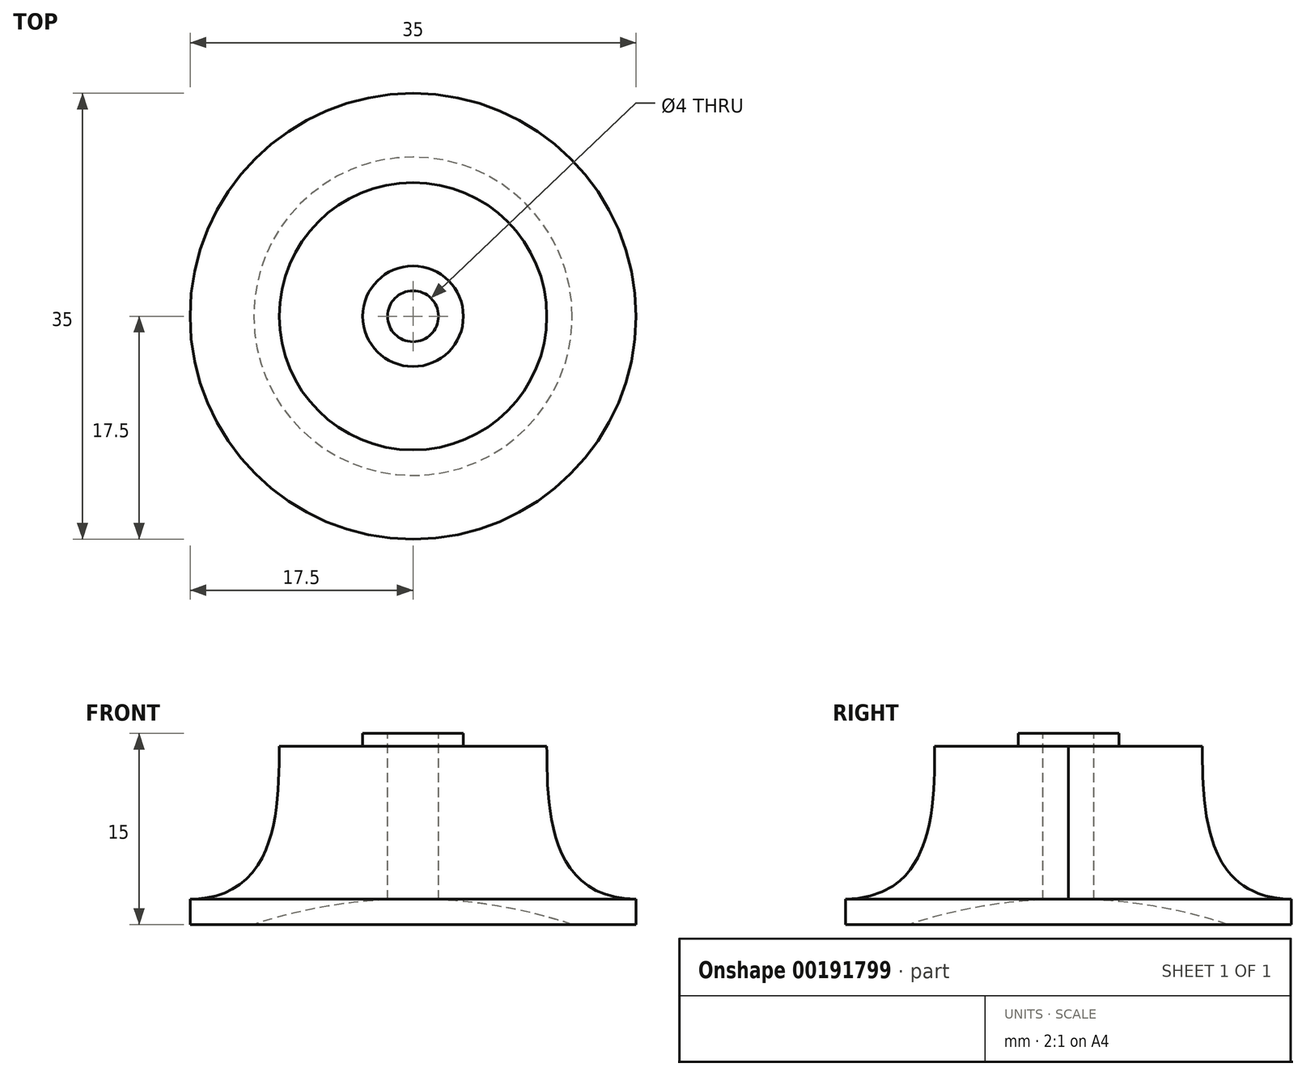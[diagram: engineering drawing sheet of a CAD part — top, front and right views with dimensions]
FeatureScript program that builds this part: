
annotation { "Feature Type Name" : "Feature", "Feature Type Description" : "" }
export const myFeature = defineFeature(function(context is Context, id is Id, definition is map)
    precondition{}
    {
        {
            var Q0;
            Q0=qCreatedBy(makeId("Front.planeOp"),FACE);
            var sketch = newSketch(context, id + "F0", { "sketchPlane" : qUnion([Q0])});
            skLineSegment(sketch, "E0", {"start": v(0, 14) * mm, "end": v(10.5, 14) * mm});
            skLineSegment(sketch, "E1", {"start": v(0, 14) * mm, "end": v(0, 0) * mm});
            skLineSegment(sketch, "E2", {"start": v(0, 2) * mm, "end": v(17.5, 2) * mm});
            skLineSegment(sketch, "E3", {"start": v(17.5, 2) * mm, "end": v(17.5, 0) * mm});
            skFitSpline(sketch, "E4", {"points": [v(17.5, 2) * mm, v(10.5, 14) * mm], "startDerivative": vector(-21.74, 0) * mm, "endDerivative": vector(-0.14, 11.7) * mm});
            skLineSegment(sketch, "E5.bottom", {"start": v(0, 14) * mm, "end": v(3.95, 14) * mm});
            skLineSegment(sketch, "E5.right", {"start": v(3.95, 14) * mm, "end": v(3.95, 15) * mm});
            skPoint(sketch, "E6", {"position": v(0, 2) * mm});
            skLineSegment(sketch, "E7", {"start": v(17.5, 0) * mm, "end": v(12.5, 0) * mm});
            skArc(sketch, "E8", {"start": v(12.5, 0) * mm, "mid": v(6.33, 1.5) * mm, "end": v(0, 2) * mm});
            skPoint(sketch, "E9", {"position": v(2, 15) * mm});
            skPoint(sketch, "E10", {"position": v(0, 15) * mm});
            skLineSegment(sketch, "E11", {"start": v(2, 15) * mm, "end": v(2.3, 15) * mm});
            skLineSegment(sketch, "E12.trimOffspring", {"start": v(0, 15) * mm, "end": v(3.95, 15) * mm});
            skLineSegment(sketch, "E13", {"start": v(0, 15) * mm, "end": v(0, 14) * mm});
            skLineSegment(sketch, "E14", {"start": v(2, 15) * mm, "end": v(2, 1.95) * mm});
            skPoint(sketch, "E15", {"position": v(2.3, 15) * mm});
            skSolve(sketch);
        }
        {
            var Q0;
            {var subQ0=sQuery(id+"F0.wireOp",EDGE,"92444a35-97c7-41ea-b5c9-697f1c7ae3100.MirrorCS");Q0=makeQuery(id+"F0.imprint","IMPRINT",FACE,{"disambiguationData":[TD([[makeQuery(id+"F0.imprint","IMPRINT",EDGE,{"derivedFrom":subQ0}),-1.0]])]});}
            var Q1;
            {var subQ3=sQuery(id+"F0.wireOp",EDGE,"5b9a50a7-b66a-4259-a33d-7a983eed8da20.MirrorCS");Q1=makeQuery(id+"F0.imprint","IMPRINT",FACE,{"disambiguationData":[TD([[makeQuery(id+"F0.imprint","IMPRINT",EDGE,{"derivedFrom":subQ3}),-1.0]])]});}
            var Q2;
            {var subQ0=sQuery(id+"F0.wireOp",EDGE,"1n8igmOa-HLYE-TCXf-oqhk-kwoFxLZ5AwYs");Q2=makeQuery(id+"F0.imprint","IMPRINT",FACE,{"disambiguationData":[TD([[makeQuery(id+"F0.imprint","IMPRINT",EDGE,{"derivedFrom":subQ0}),-1.0]])]});}
            var Q3;
            {var subQ1=sQuery(id+"F0.wireOp",EDGE,"HLsEgyHP-1YoE-nVIB-k3WF-xcQnN4NmksgT");Q3=makeQuery(id+"F0.imprint","IMPRINT",FACE,{"disambiguationData":[TD([[makeQuery(id+"F0.imprint","IMPRINT",EDGE,{"derivedFrom":subQ1}),1.0]])]});}
            var Q4;
            {var subQ0=sQuery(id+"F0.wireOp",EDGE,"E4");Q4=makeQuery(id+"F0.imprint","IMPRINT",FACE,{"disambiguationData":[TD([[makeQuery(id+"F0.imprint","IMPRINT",EDGE,{"derivedFrom":subQ0}),1.0]])]});}
            var Q5;
            {var subQ0=sQuery(id+"F0.wireOp",EDGE,"E3");Q5=makeQuery(id+"F0.imprint","IMPRINT",FACE,{"disambiguationData":[TD([[makeQuery(id+"F0.imprint","IMPRINT",EDGE,{"derivedFrom":subQ0}),-1.0]])]});}
            var Q6;
            {var subQ4=sQuery(id+"F0.wireOp",EDGE,"E5.left");Q6=makeQuery(id+"F0.imprint","IMPRINT",FACE,{"disambiguationData":[TD([[makeQuery(id+"F0.imprint","IMPRINT",EDGE,{"derivedFrom":subQ4}),-1.0]])]});}
            var Q7;
            {var subQ0=sQuery(id+"F0.wireOp",EDGE,"48ae81a1-be41-4c30-9d2b-e35cf5ec410c0.MirrorCS");Q7=makeQuery(id+"F0.imprint","IMPRINT",FACE,{"disambiguationData":[TD([[makeQuery(id+"F0.imprint","IMPRINT",EDGE,{"derivedFrom":subQ0}),-1.0]])]});}
            var Q8;
            {var subQ0=sQuery(id+"F0.wireOp",EDGE,"eHVUKEeF-jOYF-vLWz-sz2u-ke2WUjAcIU6N");Q8=makeQuery(id+"F0.imprint","IMPRINT",FACE,{"disambiguationData":[TD([[makeQuery(id+"F0.imprint","IMPRINT",EDGE,{"derivedFrom":subQ0}),1.0]])]});}
            var Q9;
            Q9=makeQuery(id+"F0.imprint","IMPRINT",FACE,{"disambiguationData":[TD([[makeQuery(id+"F0.imprint","IMPRINT",EDGE,{"derivedFrom":sQuery(id+"F0.wireOp",EDGE,"E5.bottom")}),1.0]])]});
            var Q10;
            {var subQ0=sQuery(id+"F0.wireOp",EDGE,"E5.right");Q10=makeQuery(id+"F0.imprint","IMPRINT",FACE,{"disambiguationData":[TD([[makeQuery(id+"F0.imprint","IMPRINT",EDGE,{"derivedFrom":subQ0}),1.0]])]});}
            var Q11;
            Q11=sQuery(id+"F0.wireOp",EDGE,"E1");
            revolve(context, id + "F1", {"entities" : qUnion([Q0, Q1, Q2, Q3, Q4, Q5, Q6, Q7, Q8, Q9, Q10]), "axis" : qUnion([Q11]), "revolveType" : RevolveType.FULL});
        }
    });
